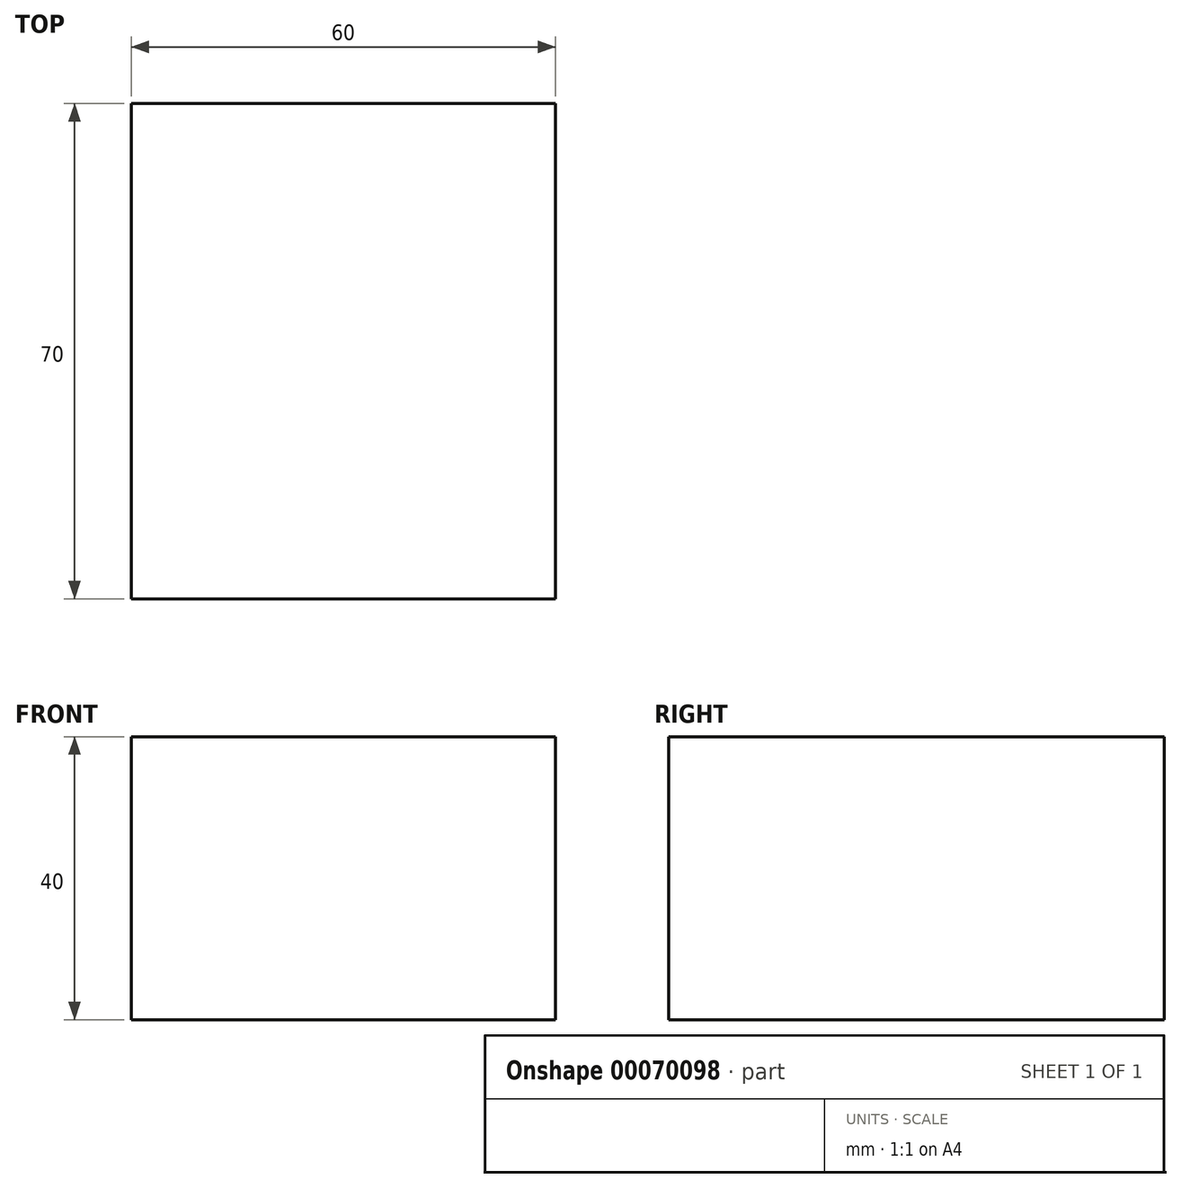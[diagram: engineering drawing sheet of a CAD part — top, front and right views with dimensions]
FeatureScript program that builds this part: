
annotation { "Feature Type Name" : "Feature", "Feature Type Description" : "" }
export const myFeature = defineFeature(function(context is Context, id is Id, definition is map)
    precondition{}
    {
        {
            var Q0;
            Q0=qCreatedBy(makeId("Front.planeOp"),FACE);
            var sketch = newSketch(context, id + "F0", { "sketchPlane" : qUnion([Q0])});
            skLineSegment(sketch, "E0.rect.bottom", {"start": v(30, 20) * mm, "end": v(-30, 20) * mm});
            skLineSegment(sketch, "E0.rect.top", {"start": v(30, -20) * mm, "end": v(-30, -20) * mm});
            skLineSegment(sketch, "E0.rect.left", {"start": v(30, 20) * mm, "end": v(30, -20) * mm});
            skLineSegment(sketch, "E0.rect.right", {"start": v(-30, 20) * mm, "end": v(-30, -20) * mm});
            skPoint(sketch, "E0.rect.middle", {"position": v(0, 0) * mm});
            skSolve(sketch);
        }
        {
            var Q0;
            Q0=makeQuery(id+"F0.imprint","IMPRINT",FACE,{"disambiguationData":[TD([[makeQuery(id+"F0.imprint","IMPRINT",EDGE,{"derivedFrom":sQuery(id+"F0.wireOp",EDGE,"E0.rect.bottom")}),1.0]])]});
            extrude(context, id + "F1", {"entities" : qUnion([Q0]), "depth" : 70 * mm});
        }
    });
